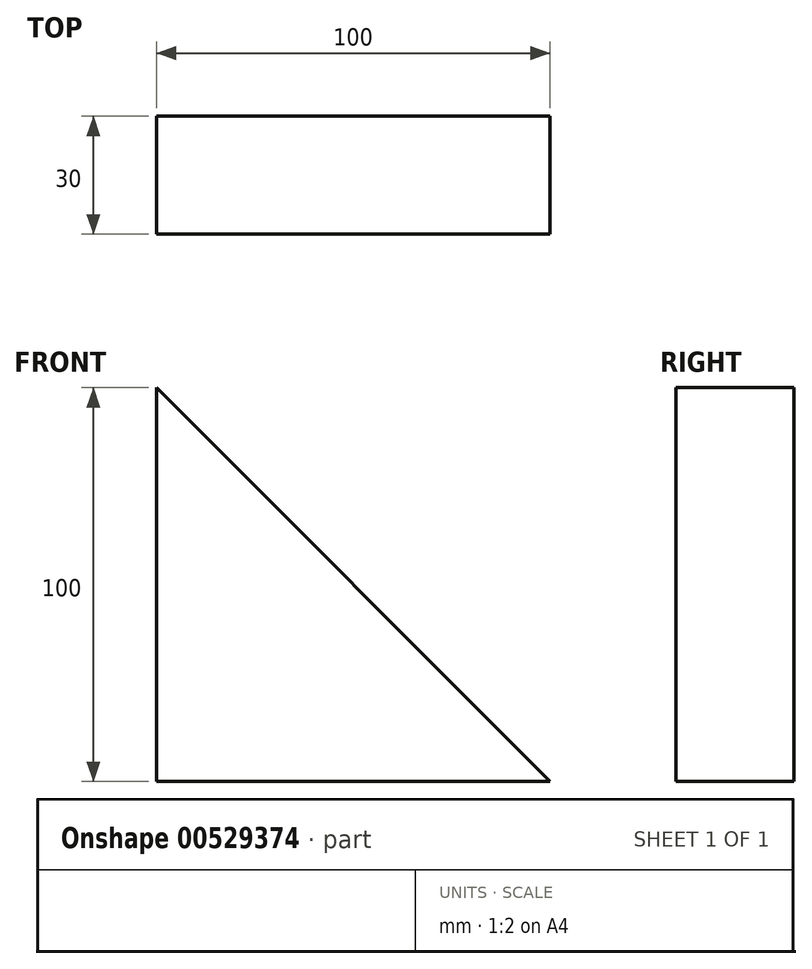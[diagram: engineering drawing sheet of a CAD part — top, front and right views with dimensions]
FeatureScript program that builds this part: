
annotation { "Feature Type Name" : "Feature", "Feature Type Description" : "" }
export const myFeature = defineFeature(function(context is Context, id is Id, definition is map)
    precondition{}
    {
        {
            var Q0;
            Q0=qCreatedBy(makeId("Front.planeOp"),FACE);
            var sketch = newSketch(context, id + "F0", { "sketchPlane" : qUnion([Q0])});
            skLineSegment(sketch, "E0", {"start": v(0, 0) * mm, "end": v(0, 100) * mm});
            skLineSegment(sketch, "E1", {"start": v(0, 100) * mm, "end": v(100, 0) * mm});
            skLineSegment(sketch, "E2", {"start": v(100, 0) * mm, "end": v(0, 0) * mm});
            skSolve(sketch);
        }
        {
            var Q0;
            Q0=makeQuery(id+"F0.imprint","IMPRINT",FACE,{"disambiguationData":[TD([[makeQuery(id+"F0.imprint","IMPRINT",EDGE,{"derivedFrom":sQuery(id+"F0.wireOp",EDGE,"E0")}),-1.0]])]});
            extrude(context, id + "F1", {"entities" : qUnion([Q0]), "endBound" : BoundingType.SYMMETRIC, "oppositeDirection" : true, "depth" : 30 * mm, "offsetDistance" : 25 * mm});
        }
    });
